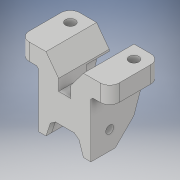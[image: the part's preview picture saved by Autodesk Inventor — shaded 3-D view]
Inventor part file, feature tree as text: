
AUTODESK INVENTOR PART (.ipt)
format: ipt  version: 2018 (Build 220112000, 112)  size: 283,136 bytes
history: native  units: in
note: dims shown in document units (in); Inventor stores cm internally (conversion verified against a paired STEP export)
features: extrude x11, sketch x11, chamfer x2, mirror x1, fillet x1, projected_geometry x1
ambient origin geometry x8: Origin, YZ Plane, XZ Plane, XY Plane, X Axis, Y Axis, Z Axis, Center Point
bodies: Solid1 (feature_tree)
feature tree (27):
  extrude  "Extrusion1"  Depth=1.1811in
  extrude  "Extrusion2"  Depth=0.1575in
  extrude  "Extrusion3"  Depth=0.3543in
  mirror  "Mirror1"
  extrude  "Extrusion4"  Depth=1.063in
  fillet  "Fillet1"  Radius=0.2756in
  chamfer  "Chamfer1"  Distance=0.3937in
  extrude  "Extrusion7"  Depth=0.1969in TaperAngle=0.0deg
  extrude  "Extrusion8"  Depth=0.3268in
  extrude  "Extrusion5"  Depth=0.3937in
  extrude  "Extrusion9"  Depth=0.2559in
  extrude  "Extrusion10"  Depth=0.1969in TaperAngle=0.0deg
  extrude  "Extrusion11"  Depth=0.0394in TaperAngle=45.0deg
  extrude  "Extrusion12"  Depth=0.1181in TaperAngle=0.0deg
  chamfer  "Chamfer2"  Distance=0.7874in
  sketch  "Sketch1"  dims[d0=0.7874in d1=1.1811in]
  sketch  "Sketch2"  dims[d2=0.1575in d3=0.1575in]
  sketch  "Sketch3"  dims[d4=0.3937in d5=0.3543in]
  sketch  "Sketch4"  dims[d6=1.063in d7=0.0in d8=0.2047in d9=0.2756in]
  sketch  "Sketch6"  dims[d10=0.2756in d11=0.3937in d12=0.0in]
  sketch  "Sketch8"  dims[d13=0.3268in d17=0.1969in d18=0.0in]
  sketch  "Sketch9"  dims[d22=0.3543in d23=0.3268in]
  sketch  "Sketch11"  dims[d24=0.1654in d25=0.3937in]
  projected_geometry  "Projected Loop1"
  sketch  "Sketch12"  dims[d27=0.1969in d28=0.0in d29=0.2559in]
  sketch  "Sketch13"  dims[d30=0.7874in d32=0.1969in d33=0.0in]
  sketch  "Sketch14"  dims[d37=0.1969in d38=0.0394in d39=0.0787in d40=45.0deg d41=0.1181in d42=0.0in d44=0.7874in d45=0.1181in d46=0.0in d47=0.3543in d48=0.1575in d49=0.1654in d50=0.1181in d51=0.0in d52=0.2756in d53=0.3543in d54=0.4724in d55=0.0in d56=0.1575in d57=0.0in d58=45.0deg d59=0.5512in d60=0.3937in d61=0.0in d62=0.2953in d63=0.1614in d64=0.1181in d65=0.1181in d66=0.3543in d67=0.3937in d68=0.0in d69=0.0787in d70=0.0787in d71=45.0deg]
